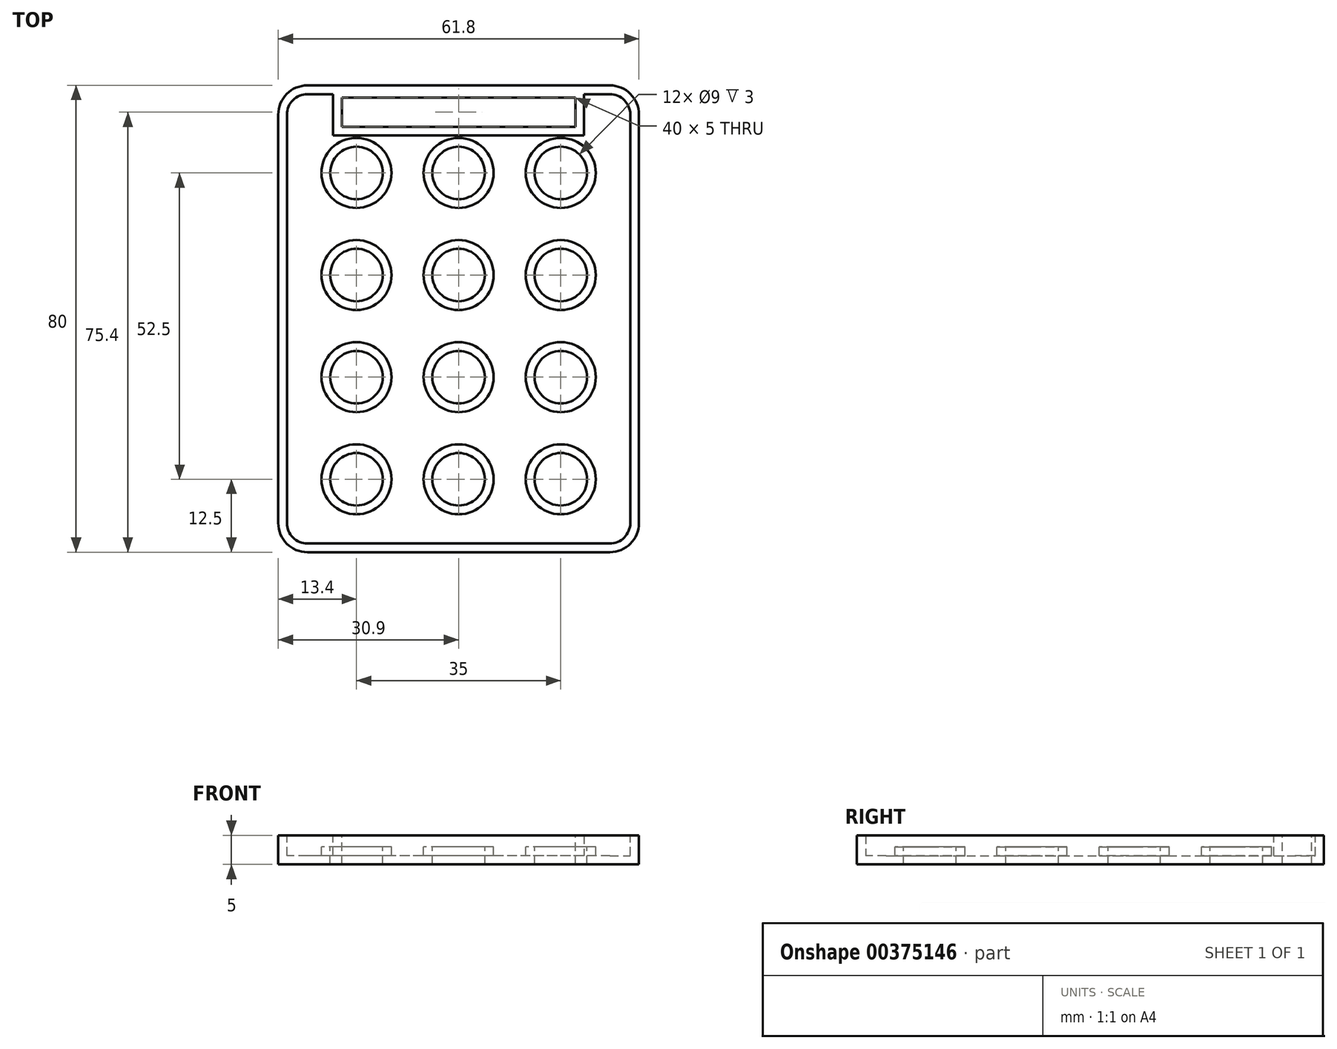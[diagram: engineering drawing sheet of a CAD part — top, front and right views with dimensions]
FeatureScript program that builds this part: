
annotation { "Feature Type Name" : "Feature", "Feature Type Description" : "" }
export const myFeature = defineFeature(function(context is Context, id is Id, definition is map)
    precondition{}
    {
        {
            var Q0;
            Q0=qCreatedBy(makeId("Top.planeOp"),FACE);
            var sketch = newSketch(context, id + "F0", { "sketchPlane" : qUnion([Q0])});
            skLineSegment(sketch, "E0.bottom", {"start": v(30.9, -40) * mm, "end": v(-30.9, -40) * mm});
            skLineSegment(sketch, "E0.top", {"start": v(30.9, 40) * mm, "end": v(-30.9, 40) * mm});
            skLineSegment(sketch, "E0.left", {"start": v(30.9, -40) * mm, "end": v(30.9, 40) * mm});
            skLineSegment(sketch, "E0.right", {"start": v(-30.9, -40) * mm, "end": v(-30.9, 40) * mm});
            skPoint(sketch, "E0.middle", {"position": v(0, 0) * mm});
            skSolve(sketch);
        }
        {
            var Q0;
            Q0 = qSketchRegion(id + "F0", true);
            var Q1;
            Q1=makeQuery(id+"F0.imprint","IMPRINT",FACE,{"disambiguationData":[TD([[makeQuery(id+"F0.imprint","IMPRINT",EDGE,{"derivedFrom":sQuery(id+"F0.wireOp",EDGE,"E0.bottom")}),-1.0]])]});
            var Q2;
            Q2 = qSketchRegion(id + "F2", true);
            extrude(context, id + "F1", {"entities" : qUnion([Q0, Q1, Q2]), "depth" : 5 * mm});
        }
        {
            var Q0;
            Q0=makeQuery(id+"F1.opExtrude","CAP_FACE",FACE,{"disambiguationData":[OSD([sQuery(id+"F0.wireOp",EDGE,"E0.bottom"),sQuery(id+"F0.wireOp",EDGE,"E0.top"),sQuery(id+"F0.wireOp",EDGE,"E0.left"),sQuery(id+"F0.wireOp",EDGE,"E0.right")])],"isStart":false});
            var sketch = newSketch(context, id + "F2", { "sketchPlane" : qUnion([Q0])});
            skLineSegment(sketch, "E1.bottom", {"start": v(20, 32.9) * mm, "end": v(-20, 32.9) * mm});
            skLineSegment(sketch, "E1.top", {"start": v(20, 37.9) * mm, "end": v(-20, 37.9) * mm});
            skLineSegment(sketch, "E1.left", {"start": v(20, 32.9) * mm, "end": v(20, 37.9) * mm});
            skLineSegment(sketch, "E1.right", {"start": v(-20, 32.9) * mm, "end": v(-20, 37.9) * mm});
            skPoint(sketch, "E1.middle", {"position": v(0, 35.4) * mm});
            skCircle(sketch, "E2", {"center": v(0, 25) * mm, "radius": 4.5 * mm});
            skLineSegment(sketch, "E3.direction1", {"start": v(0, 25) * mm, "end": v(17.5, 25) * mm, "construction": true});
            skCircle(sketch, "E4.0.1.0", {"center": v(17.5, 25) * mm, "radius": 4.5 * mm});
            skCircle(sketch, "E5.1.0.0", {"center": v(-17.5, 25) * mm, "radius": 4.5 * mm});
            skLineSegment(sketch, "E5.direction1", {"start": v(0, 25) * mm, "end": v(-17.5, 25) * mm, "construction": true});
            skCircle(sketch, "E6.0.1.0", {"center": v(-17.5, 7.5) * mm, "radius": 4.5 * mm});
            skCircle(sketch, "E6.0.1.1", {"center": v(0, 7.5) * mm, "radius": 4.5 * mm});
            skCircle(sketch, "E6.0.1.2", {"center": v(17.5, 7.5) * mm, "radius": 4.5 * mm});
            skCircle(sketch, "E6.0.2.0", {"center": v(-17.5, -10) * mm, "radius": 4.5 * mm});
            skCircle(sketch, "E6.0.2.1", {"center": v(0, -10) * mm, "radius": 4.5 * mm});
            skCircle(sketch, "E6.0.2.2", {"center": v(17.5, -10) * mm, "radius": 4.5 * mm});
            skCircle(sketch, "E6.0.3.0", {"center": v(-17.5, -27.5) * mm, "radius": 4.5 * mm});
            skCircle(sketch, "E6.0.3.1", {"center": v(0, -27.5) * mm, "radius": 4.5 * mm});
            skCircle(sketch, "E6.0.3.2", {"center": v(17.5, -27.5) * mm, "radius": 4.5 * mm});
            skLineSegment(sketch, "E6.direction1", {"start": v(-17.5, 25) * mm, "end": v(-11.6, 25) * mm, "construction": true});
            skLineSegment(sketch, "E6.direction2", {"start": v(-17.5, 25) * mm, "end": v(-17.5, 7.5) * mm, "construction": true});
            skSolve(sketch);
        }
        {
            var Q0;
            Q0=makeQuery(id+"F2.imprint","IMPRINT",FACE,{"disambiguationData":[TD([[makeQuery(id+"F2.imprint","IMPRINT",EDGE,{"derivedFrom":sQuery(id+"F2.wireOp",EDGE,"E4.0.1.0")}),1.0]])]});
            var Q1;
            Q1=makeQuery(id+"F2.imprint","IMPRINT",FACE,{"disambiguationData":[TD([[makeQuery(id+"F2.imprint","IMPRINT",EDGE,{"derivedFrom":sQuery(id+"F2.wireOp",EDGE,"E6.0.1.2")}),1.0]])]});
            var Q2;
            Q2=makeQuery(id+"F2.imprint","IMPRINT",FACE,{"disambiguationData":[TD([[makeQuery(id+"F2.imprint","IMPRINT",EDGE,{"derivedFrom":sQuery(id+"F2.wireOp",EDGE,"E6.0.1.1")}),1.0]])]});
            var Q3;
            Q3=makeQuery(id+"F2.imprint","IMPRINT",FACE,{"disambiguationData":[TD([[makeQuery(id+"F2.imprint","IMPRINT",EDGE,{"derivedFrom":sQuery(id+"F2.wireOp",EDGE,"E6.0.1.0")}),1.0]])]});
            var Q4;
            Q4=makeQuery(id+"F2.imprint","IMPRINT",FACE,{"disambiguationData":[TD([[makeQuery(id+"F2.imprint","IMPRINT",EDGE,{"derivedFrom":sQuery(id+"F2.wireOp",EDGE,"E6.0.2.0")}),1.0]])]});
            var Q5;
            Q5=makeQuery(id+"F2.imprint","IMPRINT",FACE,{"disambiguationData":[TD([[makeQuery(id+"F2.imprint","IMPRINT",EDGE,{"derivedFrom":sQuery(id+"F2.wireOp",EDGE,"E6.0.2.2")}),1.0]])]});
            var Q6;
            Q6=makeQuery(id+"F2.imprint","IMPRINT",FACE,{"disambiguationData":[TD([[makeQuery(id+"F2.imprint","IMPRINT",EDGE,{"derivedFrom":sQuery(id+"F2.wireOp",EDGE,"E6.0.3.2")}),1.0]])]});
            var Q7;
            Q7=makeQuery(id+"F2.imprint","IMPRINT",FACE,{"disambiguationData":[TD([[makeQuery(id+"F2.imprint","IMPRINT",EDGE,{"derivedFrom":sQuery(id+"F2.wireOp",EDGE,"E6.0.3.1")}),1.0]])]});
            var Q8;
            Q8=makeQuery(id+"F2.imprint","IMPRINT",FACE,{"disambiguationData":[TD([[makeQuery(id+"F2.imprint","IMPRINT",EDGE,{"derivedFrom":sQuery(id+"F2.wireOp",EDGE,"E6.0.3.0")}),1.0]])]});
            var Q9;
            Q9=makeQuery(id+"F2.imprint","IMPRINT",FACE,{"disambiguationData":[TD([[makeQuery(id+"F2.imprint","IMPRINT",EDGE,{"derivedFrom":sQuery(id+"F2.wireOp",EDGE,"E6.0.2.1")}),1.0]])]});
            var Q10;
            Q10=makeQuery(id+"F2.imprint","IMPRINT",FACE,{"disambiguationData":[TD([[makeQuery(id+"F2.imprint","IMPRINT",EDGE,{"derivedFrom":sQuery(id+"F2.wireOp",EDGE,"E5.1.0.0")}),1.0]])]});
            var Q11;
            Q11=makeQuery(id+"F2.imprint","IMPRINT",FACE,{"disambiguationData":[TD([[makeQuery(id+"F2.imprint","IMPRINT",EDGE,{"derivedFrom":sQuery(id+"F2.wireOp",EDGE,"E2")}),1.0]])]});
            var Q12;
            Q12=makeQuery(id+"F2.imprint","IMPRINT",FACE,{"disambiguationData":[TD([[makeQuery(id+"F2.imprint","IMPRINT",EDGE,{"derivedFrom":sQuery(id+"F2.wireOp",EDGE,"E1.bottom")}),-1.0]])]});
            extrude(context, id + "F3", {"entities" : qUnion([Q0, Q1, Q2, Q3, Q4, Q5, Q6, Q7, Q8, Q9, Q10, Q11, Q12]), "operationType" : NewBodyOperationType.REMOVE, "oppositeDirection" : true, "depth" : 25 * mm});
        }
        {
            var Q0;
            Q0=makeQuery(id+"F1.opExtrude","SWEPT_EDGE",EDGE,{"disambiguationData":[OSD([sQuery(id+"F0.wireOp",EDGE,"E0.top"),sQuery(id+"F0.wireOp",EDGE,"E0.right")])]});
            var Q1;
            Q1=makeQuery(id+"F1.opExtrude","SWEPT_EDGE",EDGE,{"disambiguationData":[OSD([sQuery(id+"F0.wireOp",EDGE,"E0.bottom"),sQuery(id+"F0.wireOp",EDGE,"E0.right")])]});
            var Q2;
            Q2=makeQuery(id+"F1.opExtrude","SWEPT_EDGE",EDGE,{"disambiguationData":[OSD([sQuery(id+"F0.wireOp",EDGE,"E0.bottom"),sQuery(id+"F0.wireOp",EDGE,"E0.left")])]});
            var Q3;
            Q3=makeQuery(id+"F1.opExtrude","SWEPT_EDGE",EDGE,{"disambiguationData":[OSD([sQuery(id+"F0.wireOp",EDGE,"E0.top"),sQuery(id+"F0.wireOp",EDGE,"E0.left")])]});
            fillet(context, id + "F4", {"entities" : qUnion([Q0, Q1, Q2, Q3]), "radius" : 5 * mm, "tangentPropagation" : true, "allowEdgeOverflow" : false});
        }
        {
            var Q0;
            Q0=makeQuery(id+"F1.opExtrude","CAP_FACE",FACE,{"disambiguationData":[OSD([sQuery(id+"F0.wireOp",EDGE,"E0.bottom"),sQuery(id+"F0.wireOp",EDGE,"E0.top"),sQuery(id+"F0.wireOp",EDGE,"E0.left"),sQuery(id+"F0.wireOp",EDGE,"E0.right")])],"isStart":false});
            shell(context, id + "F5", {"entities" : qUnion([Q0]), "thickness" : 1.5 * mm});
        }
        {
            var Q0;
            {var subQ0=sQuery(id+"F0.wireOp",EDGE,"E0.right");var subQ1=sQuery(id+"F0.wireOp",EDGE,"E0.left");var subQ2=sQuery(id+"F0.wireOp",EDGE,"E0.top");var subQ3=sQuery(id+"F0.wireOp",EDGE,"E0.bottom");Q0=makeQuery(id+"F5.opShell","OFFSET_FACE",FACE,{"disambiguationData":[OSD([subQ3,subQ2,subQ1,subQ0]),TDD([makeQuery(id+"F1.opExtrude","CAP_FACE",FACE,{"disambiguationData":[OSD([subQ3,subQ2,subQ1,subQ0])],"isStart":false})]),OD(1.0)]});}
            var Q1;
            {var subQ0=sQuery(id+"F0.wireOp",EDGE,"E0.right");var subQ1=sQuery(id+"F0.wireOp",EDGE,"E0.left");var subQ2=sQuery(id+"F0.wireOp",EDGE,"E0.top");var subQ3=sQuery(id+"F0.wireOp",EDGE,"E0.bottom");Q1=makeQuery(id+"F5.opShell","OFFSET_FACE",FACE,{"disambiguationData":[OSD([subQ3,subQ2,subQ1,subQ0]),TDD([makeQuery(id+"F1.opExtrude","CAP_FACE",FACE,{"disambiguationData":[OSD([subQ3,subQ2,subQ1,subQ0])],"isStart":false})]),OD(0.0)]});}
            var Q2;
            {var subQ0=sQuery(id+"F0.wireOp",EDGE,"E0.right");var subQ1=sQuery(id+"F0.wireOp",EDGE,"E0.left");var subQ2=sQuery(id+"F0.wireOp",EDGE,"E0.top");var subQ3=sQuery(id+"F0.wireOp",EDGE,"E0.bottom");Q2=makeQuery(id+"F5.opShell","OFFSET_FACE",FACE,{"disambiguationData":[OSD([subQ3,subQ2,subQ1,subQ0]),TDD([makeQuery(id+"F1.opExtrude","CAP_FACE",FACE,{"disambiguationData":[OSD([subQ3,subQ2,subQ1,subQ0])],"isStart":false})]),OD(4.0)]});}
            var Q3;
            {var subQ0=sQuery(id+"F0.wireOp",EDGE,"E0.right");var subQ1=sQuery(id+"F0.wireOp",EDGE,"E0.left");var subQ2=sQuery(id+"F0.wireOp",EDGE,"E0.top");var subQ3=sQuery(id+"F0.wireOp",EDGE,"E0.bottom");Q3=makeQuery(id+"F5.opShell","OFFSET_FACE",FACE,{"disambiguationData":[OSD([subQ3,subQ2,subQ1,subQ0]),TDD([makeQuery(id+"F1.opExtrude","CAP_FACE",FACE,{"disambiguationData":[OSD([subQ3,subQ2,subQ1,subQ0])],"isStart":false})]),OD(5.0)]});}
            var Q4;
            {var subQ0=sQuery(id+"F0.wireOp",EDGE,"E0.right");var subQ1=sQuery(id+"F0.wireOp",EDGE,"E0.left");var subQ2=sQuery(id+"F0.wireOp",EDGE,"E0.top");var subQ3=sQuery(id+"F0.wireOp",EDGE,"E0.bottom");Q4=makeQuery(id+"F5.opShell","OFFSET_FACE",FACE,{"disambiguationData":[OSD([subQ3,subQ2,subQ1,subQ0]),TDD([makeQuery(id+"F1.opExtrude","CAP_FACE",FACE,{"disambiguationData":[OSD([subQ3,subQ2,subQ1,subQ0])],"isStart":false})]),OD(2.0)]});}
            var Q5;
            {var subQ0=sQuery(id+"F0.wireOp",EDGE,"E0.right");var subQ1=sQuery(id+"F0.wireOp",EDGE,"E0.left");var subQ2=sQuery(id+"F0.wireOp",EDGE,"E0.top");var subQ3=sQuery(id+"F0.wireOp",EDGE,"E0.bottom");Q5=makeQuery(id+"F5.opShell","OFFSET_FACE",FACE,{"disambiguationData":[OSD([subQ3,subQ2,subQ1,subQ0]),TDD([makeQuery(id+"F1.opExtrude","CAP_FACE",FACE,{"disambiguationData":[OSD([subQ3,subQ2,subQ1,subQ0])],"isStart":false})]),OD(3.0)]});}
            var Q6;
            {var subQ0=sQuery(id+"F0.wireOp",EDGE,"E0.right");var subQ1=sQuery(id+"F0.wireOp",EDGE,"E0.left");var subQ2=sQuery(id+"F0.wireOp",EDGE,"E0.top");var subQ3=sQuery(id+"F0.wireOp",EDGE,"E0.bottom");Q6=makeQuery(id+"F5.opShell","OFFSET_FACE",FACE,{"disambiguationData":[OSD([subQ3,subQ2,subQ1,subQ0]),TDD([makeQuery(id+"F1.opExtrude","CAP_FACE",FACE,{"disambiguationData":[OSD([subQ3,subQ2,subQ1,subQ0])],"isStart":false})]),OD(6.0)]});}
            var Q7;
            {var subQ0=sQuery(id+"F0.wireOp",EDGE,"E0.right");var subQ1=sQuery(id+"F0.wireOp",EDGE,"E0.left");var subQ2=sQuery(id+"F0.wireOp",EDGE,"E0.top");var subQ3=sQuery(id+"F0.wireOp",EDGE,"E0.bottom");Q7=makeQuery(id+"F5.opShell","OFFSET_FACE",FACE,{"disambiguationData":[OSD([subQ3,subQ2,subQ1,subQ0]),TDD([makeQuery(id+"F1.opExtrude","CAP_FACE",FACE,{"disambiguationData":[OSD([subQ3,subQ2,subQ1,subQ0])],"isStart":false})]),OD(7.0)]});}
            var Q8;
            {var subQ0=sQuery(id+"F0.wireOp",EDGE,"E0.right");var subQ1=sQuery(id+"F0.wireOp",EDGE,"E0.left");var subQ2=sQuery(id+"F0.wireOp",EDGE,"E0.top");var subQ3=sQuery(id+"F0.wireOp",EDGE,"E0.bottom");Q8=makeQuery(id+"F5.opShell","OFFSET_FACE",FACE,{"disambiguationData":[OSD([subQ3,subQ2,subQ1,subQ0]),TDD([makeQuery(id+"F1.opExtrude","CAP_FACE",FACE,{"disambiguationData":[OSD([subQ3,subQ2,subQ1,subQ0])],"isStart":false})]),OD(8.0)]});}
            var Q9;
            {var subQ0=sQuery(id+"F0.wireOp",EDGE,"E0.right");var subQ1=sQuery(id+"F0.wireOp",EDGE,"E0.left");var subQ2=sQuery(id+"F0.wireOp",EDGE,"E0.top");var subQ3=sQuery(id+"F0.wireOp",EDGE,"E0.bottom");Q9=makeQuery(id+"F5.opShell","OFFSET_FACE",FACE,{"disambiguationData":[OSD([subQ3,subQ2,subQ1,subQ0]),TDD([makeQuery(id+"F1.opExtrude","CAP_FACE",FACE,{"disambiguationData":[OSD([subQ3,subQ2,subQ1,subQ0])],"isStart":false})]),OD(9.0)]});}
            var Q10;
            {var subQ0=sQuery(id+"F0.wireOp",EDGE,"E0.right");var subQ1=sQuery(id+"F0.wireOp",EDGE,"E0.left");var subQ2=sQuery(id+"F0.wireOp",EDGE,"E0.top");var subQ3=sQuery(id+"F0.wireOp",EDGE,"E0.bottom");Q10=makeQuery(id+"F5.opShell","OFFSET_FACE",FACE,{"disambiguationData":[OSD([subQ3,subQ2,subQ1,subQ0]),TDD([makeQuery(id+"F1.opExtrude","CAP_FACE",FACE,{"disambiguationData":[OSD([subQ3,subQ2,subQ1,subQ0])],"isStart":false})]),OD(10.0)]});}
            var Q11;
            {var subQ0=sQuery(id+"F0.wireOp",EDGE,"E0.right");var subQ1=sQuery(id+"F0.wireOp",EDGE,"E0.left");var subQ2=sQuery(id+"F0.wireOp",EDGE,"E0.top");var subQ3=sQuery(id+"F0.wireOp",EDGE,"E0.bottom");Q11=makeQuery(id+"F5.opShell","OFFSET_FACE",FACE,{"disambiguationData":[OSD([subQ3,subQ2,subQ1,subQ0]),TDD([makeQuery(id+"F1.opExtrude","CAP_FACE",FACE,{"disambiguationData":[OSD([subQ3,subQ2,subQ1,subQ0])],"isStart":false})]),OD(11.0)]});}
            extrude(context, id + "F6", {"entities" : qUnion([Q0, Q1, Q2, Q3, Q4, Q5, Q6, Q7, Q8, Q9, Q10, Q11]), "operationType" : NewBodyOperationType.REMOVE, "oppositeDirection" : true, "depth" : 2 * mm});
        }
    });
